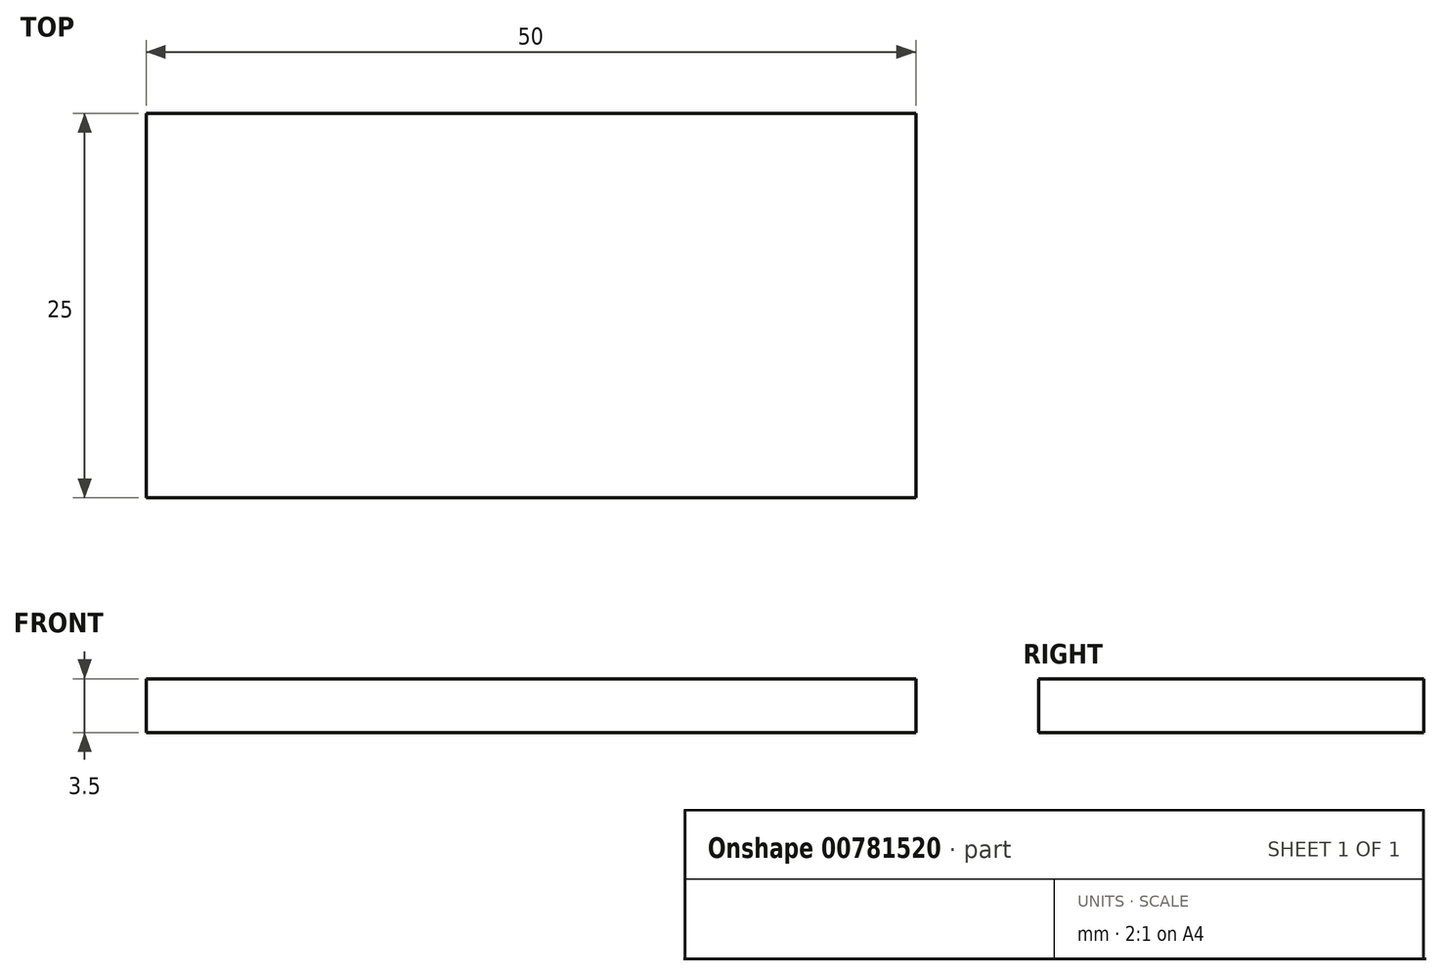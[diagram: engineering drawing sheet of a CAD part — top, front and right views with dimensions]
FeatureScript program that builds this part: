
annotation { "Feature Type Name" : "Feature", "Feature Type Description" : "" }
export const myFeature = defineFeature(function(context is Context, id is Id, definition is map)
    precondition{}
    {
        {
            var Q0;
            Q0=qCreatedBy(makeId("Front.planeOp"),FACE);
            var sketch = newSketch(context, id + "F0", { "sketchPlane" : qUnion([Q0])});
            skLineSegment(sketch, "E0.bottom", {"start": v(0, 0) * mm, "end": v(50, 0) * mm});
            skLineSegment(sketch, "E0.top", {"start": v(0, 3.5) * mm, "end": v(50, 3.5) * mm});
            skLineSegment(sketch, "E0.left", {"start": v(0, 0) * mm, "end": v(0, 3.5) * mm});
            skLineSegment(sketch, "E0.right", {"start": v(50, 0) * mm, "end": v(50, 3.5) * mm});
            skSolve(sketch);
        }
        {
            var Q0;
            Q0 = qSketchRegion(id + "F0", true);
            extrude(context, id + "F1", {"entities" : qUnion([Q0]), "depth" : 25 * mm, "offsetDistance" : 25 * mm});
        }
    });
